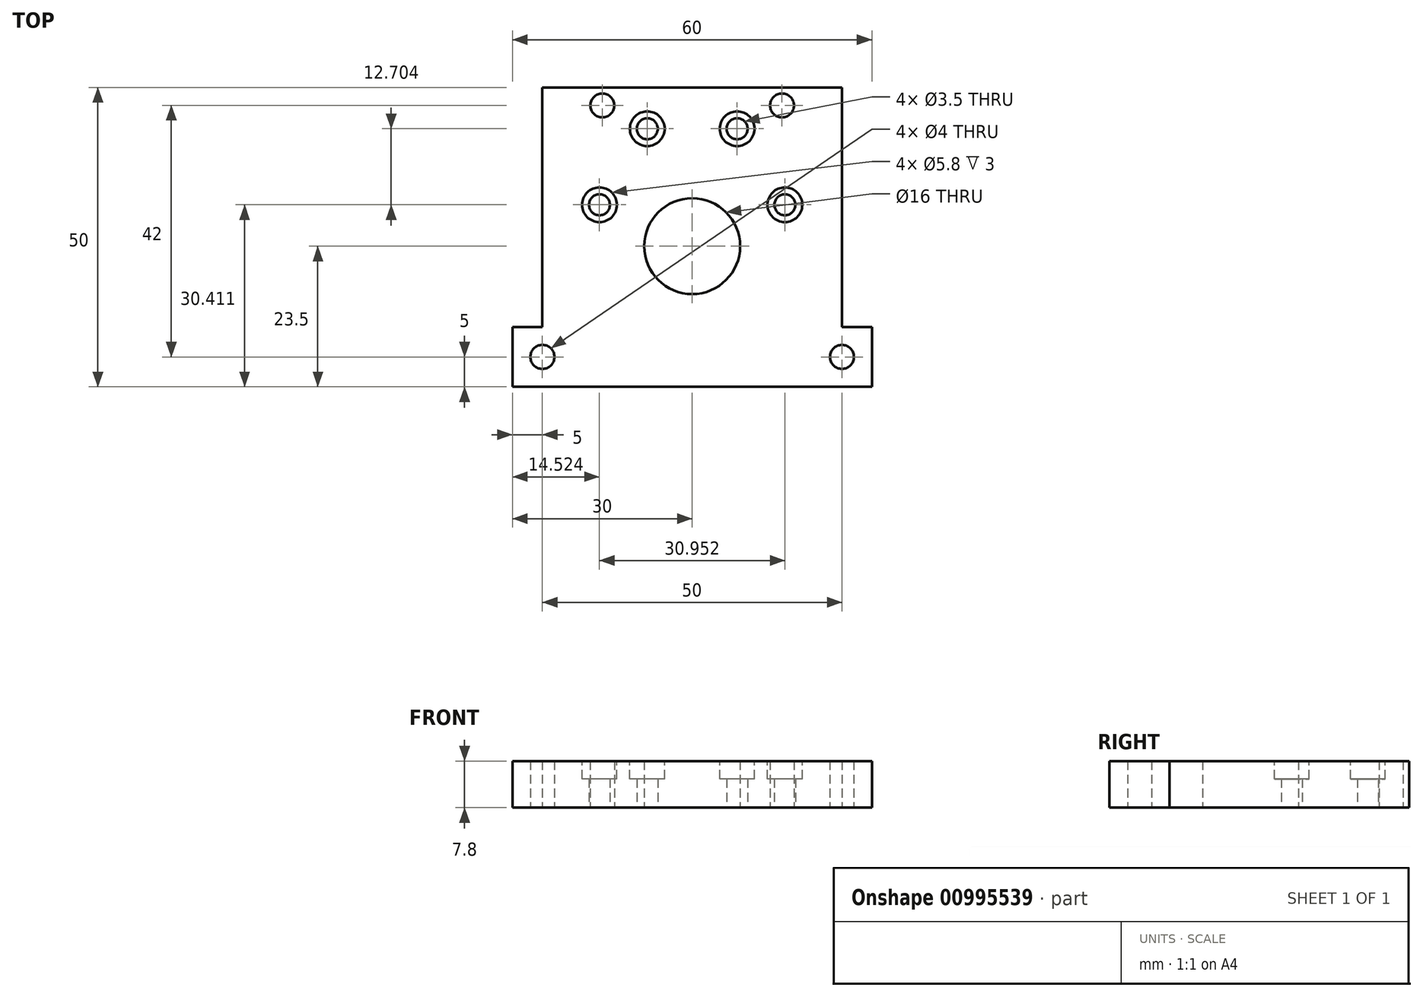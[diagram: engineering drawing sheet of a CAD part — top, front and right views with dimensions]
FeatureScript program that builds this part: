
annotation { "Feature Type Name" : "Feature", "Feature Type Description" : "" }
export const myFeature = defineFeature(function(context is Context, id is Id, definition is map)
    precondition{}
    {
        {
            var Q0;
            Q0=qCreatedBy(makeId("Top.planeOp"),FACE);
            var sketch = newSketch(context, id + "F0", { "sketchPlane" : qUnion([Q0])});
            skLineSegment(sketch, "E0.bottom", {"start": v(25, -23.5) * mm, "end": v(-25, -23.5) * mm});
            skLineSegment(sketch, "E0.top", {"start": v(25, 26.5) * mm, "end": v(-25, 26.5) * mm});
            skLineSegment(sketch, "E0.left", {"start": v(25, -13.5) * mm, "end": v(25, 26.5) * mm});
            skLineSegment(sketch, "E0.right", {"start": v(-25, -13.5) * mm, "end": v(-25, 26.5) * mm});
            skPoint(sketch, "E0.middle", {"position": v(0, 0) * mm});
            skLineSegment(sketch, "E1.bottom", {"start": v(-25, -23.5) * mm, "end": v(-30, -23.5) * mm});
            skLineSegment(sketch, "E1.top", {"start": v(-25, -13.5) * mm, "end": v(-30, -13.5) * mm});
            skLineSegment(sketch, "E1.right", {"start": v(-30, -23.5) * mm, "end": v(-30, -13.5) * mm});
            skLineSegment(sketch, "E2.bottom", {"start": v(25, -23.5) * mm, "end": v(30, -23.5) * mm});
            skLineSegment(sketch, "E2.top", {"start": v(25, -13.5) * mm, "end": v(30, -13.5) * mm});
            skLineSegment(sketch, "E2.right", {"start": v(30, -23.5) * mm, "end": v(30, -13.5) * mm});
            skCircle(sketch, "E3", {"center": v(0, 0) * mm, "radius": 8 * mm});
            skCircle(sketch, "E4", {"center": v(-7.5, 19.62) * mm, "radius": 1.75 * mm});
            skCircle(sketch, "E5", {"center": v(-25, -18.5) * mm, "radius": 2 * mm});
            skPoint(sketch, "E5.centerSnap0", {"position": v(-30, -18.5) * mm});
            skCircle(sketch, "E6", {"center": v(25, -18.5) * mm, "radius": 2 * mm});
            skPoint(sketch, "E7.center", {"position": v(0, -11.35) * mm});
            skCircle(sketch, "E8", {"center": v(-15, 23.5) * mm, "radius": 2 * mm});
            skCircle(sketch, "E9", {"center": v(15, 23.5) * mm, "radius": 2 * mm});
            skCircle(sketch, "E10", {"center": v(0, 0) * mm, "radius": 21 * mm, "construction": true});
            skCircle(sketch, "E11", {"center": v(7.5, 19.62) * mm, "radius": 1.75 * mm});
            skCircle(sketch, "E12", {"center": v(-15.48, 6.91) * mm, "radius": 1.75 * mm});
            skCircle(sketch, "E13", {"center": v(15.48, 6.91) * mm, "radius": 1.75 * mm});
            skCircle(sketch, "E14", {"center": v(0, 6.05) * mm, "radius": 15.5 * mm, "construction": true});
            skSolve(sketch);
        }
        {
            var Q0;
            Q0=makeQuery(id+"F0.imprint","IMPRINT",FACE,{"disambiguationData":[TD([[makeQuery(id+"F0.imprint","IMPRINT",EDGE,{"derivedFrom":sQuery(id+"F0.wireOp",EDGE,"E0.bottom")}),-1.0]])]});
            extrude(context, id + "F1", {"entities" : qUnion([Q0]), "depth" : 7.8 * mm, "offsetDistance" : 25 * mm});
        }
        {
            var Q0;
            Q0=makeQuery(id+"F1.opExtrude","CAP_FACE",FACE,{"disambiguationData":[OSD([sQuery(id+"F0.wireOp",EDGE,"E0.bottom"),sQuery(id+"F0.wireOp",EDGE,"E0.top"),sQuery(id+"F0.wireOp",EDGE,"E0.left"),sQuery(id+"F0.wireOp",EDGE,"E0.right"),sQuery(id+"F0.wireOp",EDGE,"E1.bottom"),sQuery(id+"F0.wireOp",EDGE,"E1.top"),sQuery(id+"F0.wireOp",EDGE,"E1.right"),sQuery(id+"F0.wireOp",EDGE,"E2.bottom"),sQuery(id+"F0.wireOp",EDGE,"E2.top"),sQuery(id+"F0.wireOp",EDGE,"E2.right"),sQuery(id+"F0.wireOp",EDGE,"E3"),sQuery(id+"F0.wireOp",EDGE,"E4"),sQuery(id+"F0.wireOp",EDGE,"E5"),sQuery(id+"F0.wireOp",EDGE,"E6"),sQuery(id+"F0.wireOp",EDGE,"E7.1.0"),sQuery(id+"F0.wireOp",EDGE,"E7.2.0"),sQuery(id+"F0.wireOp",EDGE,"E7.3.0"),sQuery(id+"F0.wireOp",EDGE,"E8"),sQuery(id+"F0.wireOp",EDGE,"E9")])],"isStart":false});
            var sketch = newSketch(context, id + "F2", { "sketchPlane" : qUnion([Q0])});
            skCircle(sketch, "E15", {"center": v(-7.5, 19.62) * mm, "radius": 2.9 * mm});
            skCircle(sketch, "E16.1.0", {"center": v(-15.48, 6.91) * mm, "radius": 2.9 * mm});
            skCircle(sketch, "E16.2.0", {"center": v(15.48, 6.91) * mm, "radius": 2.9 * mm});
            skCircle(sketch, "E16.3.0", {"center": v(7.5, 19.62) * mm, "radius": 2.9 * mm});
            skPoint(sketch, "E16.center", {"position": v(0, 0) * mm});
            skSolve(sketch);
        }
        {
            var Q0;
            Q0=makeQuery(id+"F2.imprint","IMPRINT",FACE,{"disambiguationData":[TD([[makeQuery(id+"F2.imprint","IMPRINT",EDGE,{"derivedFrom":sQuery(id+"F2.wireOp",EDGE,"E15")}),1.0]])]});
            var Q1;
            Q1=makeQuery(id+"F2.imprint","IMPRINT",FACE,{"disambiguationData":[TD([[makeQuery(id+"F2.imprint","IMPRINT",EDGE,{"derivedFrom":sQuery(id+"F2.wireOp",EDGE,"E16.3.0")}),1.0]])]});
            var Q2;
            Q2=makeQuery(id+"F2.imprint","IMPRINT",FACE,{"disambiguationData":[TD([[makeQuery(id+"F2.imprint","IMPRINT",EDGE,{"derivedFrom":sQuery(id+"F2.wireOp",EDGE,"E16.2.0")}),1.0]])]});
            var Q3;
            Q3=makeQuery(id+"F2.imprint","IMPRINT",FACE,{"disambiguationData":[TD([[makeQuery(id+"F2.imprint","IMPRINT",EDGE,{"derivedFrom":sQuery(id+"F2.wireOp",EDGE,"E16.1.0")}),1.0]])]});
            extrude(context, id + "F3", {"entities" : qUnion([Q0, Q1, Q2, Q3]), "operationType" : NewBodyOperationType.REMOVE, "oppositeDirection" : true, "depth" : 3 * mm, "offsetDistance" : 25 * mm});
        }
    });
